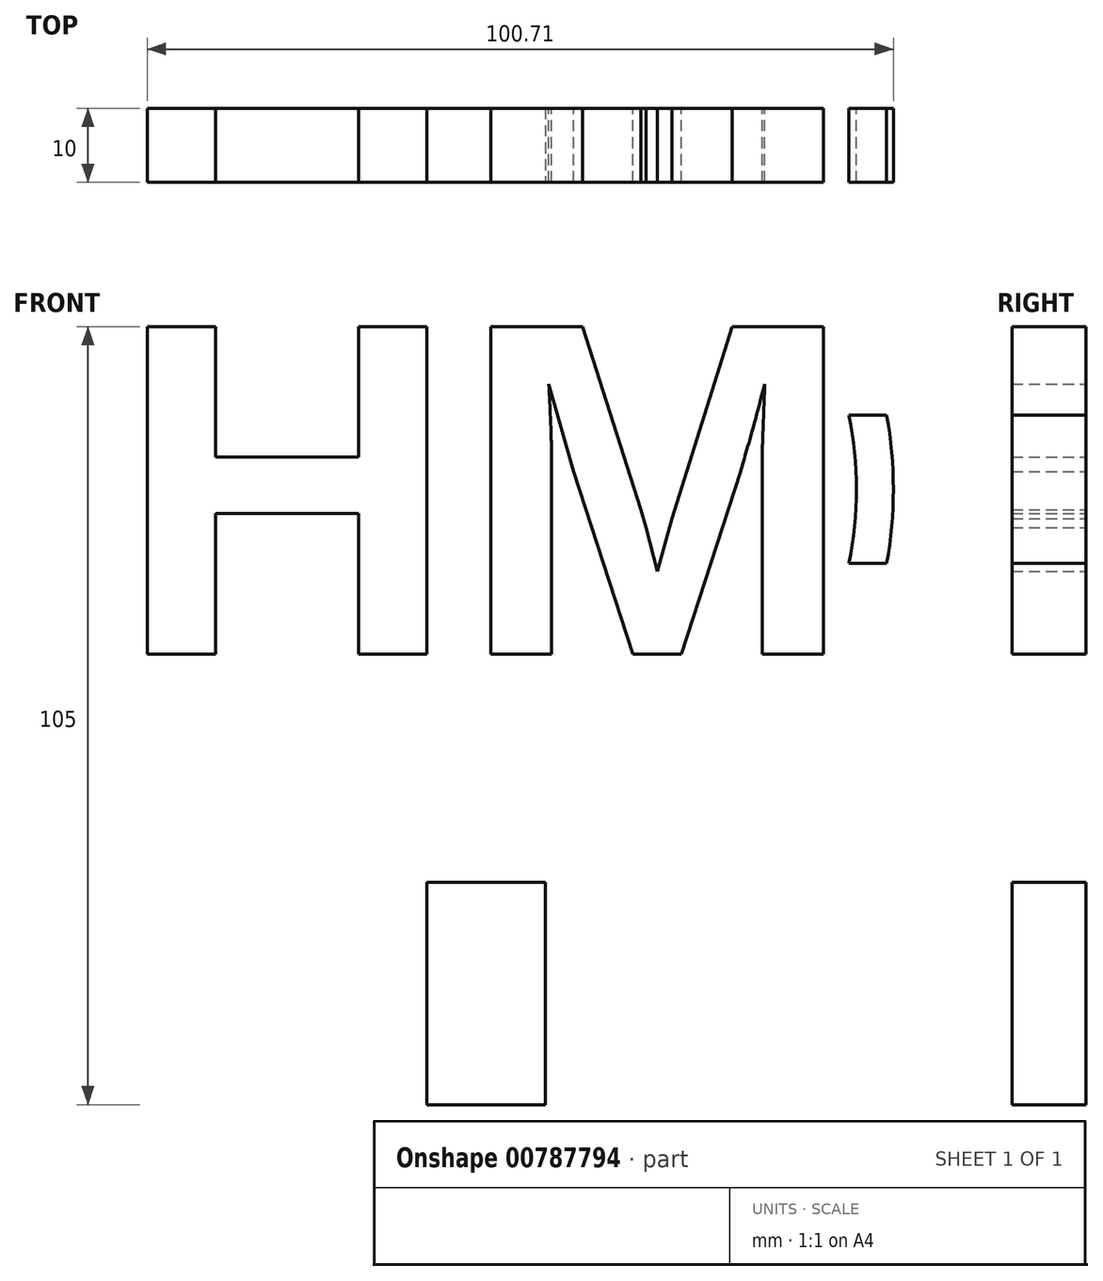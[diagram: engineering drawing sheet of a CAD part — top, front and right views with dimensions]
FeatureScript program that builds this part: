
annotation { "Feature Type Name" : "Feature", "Feature Type Description" : "" }
export const myFeature = defineFeature(function(context is Context, id is Id, definition is map)
    precondition{}
    {
        {
            var Q0;
            Q0=qCreatedBy(makeId("Front.planeOp"),FACE);
            var sketch = newSketch(context, id + "F0", { "sketchPlane" : qUnion([Q0])});
            skText(sketch, "E0", { "text": "HM", "fontName": "Arimo-Bold.ttf"});
            const initialGuessF0  = {"E0": [-0.05, -0.04622, 1, 0, 0.04622]};
            skSetInitialGuess(sketch, initialGuessF0);
            skSolve(sketch);
        }
        {
            var Q0;
            Q0 = qSketchRegion(id + "F0", true);
            extrude(context, id + "F1", {"entities" : qUnion([Q0]), "depth" : 10 * mm, "offsetDistance" : 25 * mm});
        }
        {
            var Q0;
            Q0=qCreatedBy(makeId("Front.planeOp"),FACE);
            var sketch = newSketch(context, id + "F2", { "sketchPlane" : qUnion([Q0])});
            skCircle(sketch, "E1", {"center": v(0, -24) * mm, "radius": 50 * mm});
            skCircle(sketch, "E2.0", {"center": v(0, -24) * mm, "radius": 55 * mm});
            skLineSegment(sketch, "E3.bottom", {"start": v(60.53, -34) * mm, "end": v(-60.53, -34) * mm});
            skLineSegment(sketch, "E3.top", {"start": v(60.53, -14) * mm, "end": v(-60.53, -14) * mm});
            skLineSegment(sketch, "E3.left", {"start": v(60.53, -34) * mm, "end": v(60.53, -14) * mm});
            skLineSegment(sketch, "E3.right", {"start": v(-60.53, -34) * mm, "end": v(-60.53, -14) * mm});
            skSolve(sketch);
        }
        {
            var Q0;
            {var subQ0=sQuery(id+"F2.wireOp",EDGE,"E3.top");var subQ1=sQuery(id+"F2.wireOp",EDGE,"E1");var subQ2=makeQuery(id+"F2.imprint","INTERSECT",VERTEX,{"disambiguationData":[OD(0.0)],"derivedFrom":[subQ1,subQ0]});Q0=makeQuery(id+"F2.imprint","IMPRINT",FACE,{"disambiguationData":[TD([[makeQuery(id+"F2.imprint","IMPRINT",EDGE,{"disambiguationData":[TD([[subQ2,1.0]])],"derivedFrom":subQ1}),-1.0]])]});}
            var Q1;
            {var subQ0=sQuery(id+"F2.wireOp",EDGE,"E3.bottom");var subQ1=sQuery(id+"F2.wireOp",EDGE,"E1");var subQ2=makeQuery(id+"F2.imprint","INTERSECT",VERTEX,{"disambiguationData":[OD(0.0)],"derivedFrom":[subQ1,subQ0]});Q1=makeQuery(id+"F2.imprint","IMPRINT",FACE,{"disambiguationData":[TD([[makeQuery(id+"F2.imprint","IMPRINT",EDGE,{"disambiguationData":[TD([[subQ2,-1.0]])],"derivedFrom":subQ1}),-1.0]])]});}
            extrude(context, id + "F3", {"entities" : qUnion([Q0, Q1]), "depth" : 10 * mm, "offsetDistance" : 25 * mm});
        }
        {
            var Q0;
            Q0=makeQuery(id+"F1.opExtrude","CAP_FACE",FACE,{"disambiguationData":[OSD([sQuery(id+"F0.wireOp",EDGE,"E0.sketch_text.stroke-0"),sQuery(id+"F0.wireOp",EDGE,"E0.sketch_text.stroke-1"),sQuery(id+"F0.wireOp",EDGE,"E0.sketch_text.stroke-2"),sQuery(id+"F0.wireOp",EDGE,"E0.sketch_text.stroke-3"),sQuery(id+"F0.wireOp",EDGE,"E0.sketch_text.stroke-4"),sQuery(id+"F0.wireOp",EDGE,"E0.sketch_text.stroke-5"),sQuery(id+"F0.wireOp",EDGE,"E0.sketch_text.stroke-6"),sQuery(id+"F0.wireOp",EDGE,"E0.sketch_text.stroke-7"),sQuery(id+"F0.wireOp",EDGE,"E0.sketch_text.stroke-8"),sQuery(id+"F0.wireOp",EDGE,"E0.sketch_text.stroke-9"),sQuery(id+"F0.wireOp",EDGE,"E0.sketch_text.stroke-10"),sQuery(id+"F0.wireOp",EDGE,"E0.sketch_text.stroke-11")])],"isStart":false});
            var sketch = newSketch(context, id + "F4", { "sketchPlane" : qUnion([Q0])});
            skLineSegment(sketch, "E4.bottom", {"start": v(8, -107.06) * mm, "end": v(-8, -107.06) * mm});
            skLineSegment(sketch, "E4.top", {"start": v(8, -77.06) * mm, "end": v(-8, -77.06) * mm});
            skLineSegment(sketch, "E4.left", {"start": v(8, -107.06) * mm, "end": v(8, -77.06) * mm});
            skLineSegment(sketch, "E4.right", {"start": v(-8, -107.06) * mm, "end": v(-8, -77.06) * mm});
            skPoint(sketch, "E4.middle", {"position": v(0, -92.06) * mm});
            skSolve(sketch);
        }
        {
            var Q0;
            Q0 = qSketchRegion(id + "F4", true);
            extrude(context, id + "F5", {"entities" : qUnion([Q0]), "operationType" : NewBodyOperationType.ADD, "oppositeDirection" : true, "depth" : 10 * mm, "offsetDistance" : 25 * mm});
        }
    });
